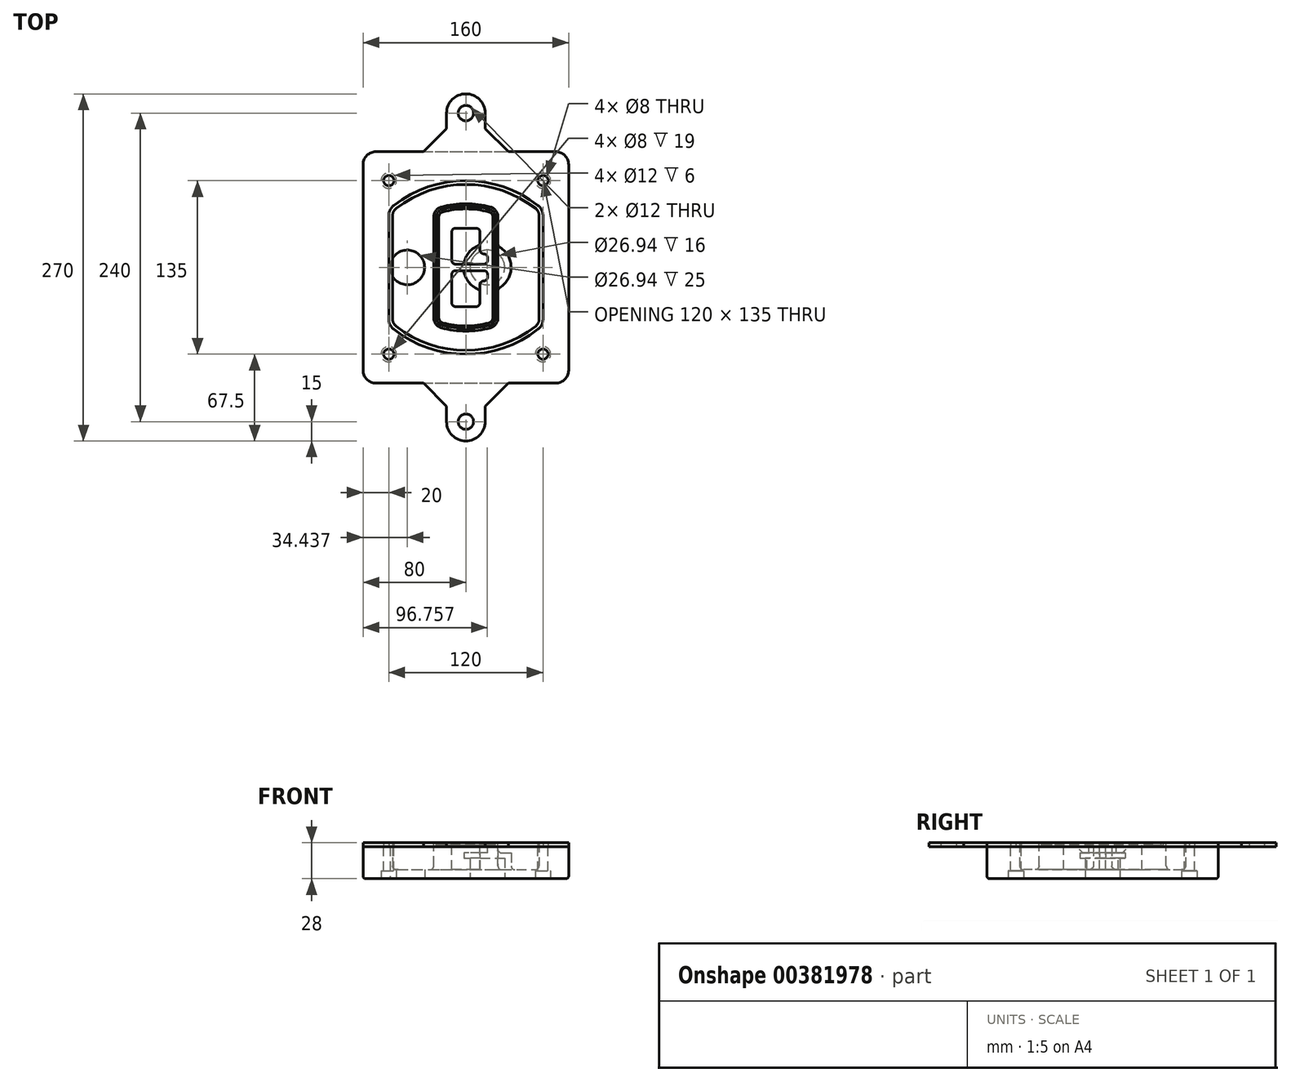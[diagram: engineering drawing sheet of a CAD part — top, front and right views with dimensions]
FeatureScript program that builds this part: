
annotation { "Feature Type Name" : "Feature", "Feature Type Description" : "" }
export const myFeature = defineFeature(function(context is Context, id is Id, definition is map)
    precondition{}
    {
        {
            var Q0;
            Q0=qCreatedBy(makeId("Top.planeOp"),FACE);
            var sketch = newSketch(context, id + "F0", { "sketchPlane" : qUnion([Q0])});
            skPoint(sketch, "E0.rect.middle", {"position": v(0, 0) * mm});
            skLineSegment(sketch, "E1.bottom", {"start": v(-70, -90) * mm, "end": v(70, -90) * mm});
            skLineSegment(sketch, "E1.top", {"start": v(-70, 90) * mm, "end": v(70, 90) * mm});
            skLineSegment(sketch, "E1.left", {"start": v(-80, -80) * mm, "end": v(-80, 80) * mm});
            skLineSegment(sketch, "E1.right", {"start": v(80, -80) * mm, "end": v(80, 80) * mm});
            skLineSegment(sketch, "E2", {"start": v(-80, 90) * mm, "end": v(80, -90) * mm, "construction": true});
            skLineSegment(sketch, "E3", {"start": v(80, 90) * mm, "end": v(-80, -90) * mm, "construction": true});
            skCircle(sketch, "E4", {"center": v(-60, 67.5) * mm, "radius": 4 * mm});
            skCircle(sketch, "E5", {"center": v(60, 67.5) * mm, "radius": 4 * mm});
            skCircle(sketch, "E6", {"center": v(60, -67.5) * mm, "radius": 4 * mm});
            skCircle(sketch, "E7", {"center": v(-60, -67.5) * mm, "radius": 4 * mm});
            skLineSegment(sketch, "E8", {"start": v(-60, 67.5) * mm, "end": v(60, 67.5) * mm, "construction": true});
            skLineSegment(sketch, "E9", {"start": v(60, 67.5) * mm, "end": v(60, -67.5) * mm, "construction": true});
            skLineSegment(sketch, "E10", {"start": v(60, -67.5) * mm, "end": v(-60, -67.5) * mm, "construction": true});
            skLineSegment(sketch, "E11", {"start": v(-60, -67.5) * mm, "end": v(-60, 67.5) * mm, "construction": true});
            skLineSegment(sketch, "E12", {"start": v(-60, 40.3) * mm, "end": v(-60, -40.3) * mm});
            skLineSegment(sketch, "E13", {"start": v(60, 40.3) * mm, "end": v(60, -40.3) * mm});
            skArc(sketch, "E14", {"start": v(56.15, 48.18) * mm, "mid": v(0, 67.5) * mm, "end": v(-56.15, 48.18) * mm});
            skArc(sketch, "E15", {"start": v(-56.15, -48.18) * mm, "mid": v(0, -67.5) * mm, "end": v(56.15, -48.18) * mm});
            skLineSegment(sketch, "E16", {"start": v(-60, 0) * mm, "end": v(60, 0) * mm, "construction": true});
            skPoint(sketch, "E17.visualSharp", {"position": v(-60, -45) * mm});
            skArc(sketch, "E17.filletArc", {"start": v(-60, -40.3) * mm, "mid": v(-58.99, -44.68) * mm, "end": v(-56.15, -48.18) * mm});
            skPoint(sketch, "E18.visualSharp", {"position": v(-60, 45) * mm});
            skArc(sketch, "E18.filletArc", {"start": v(-56.15, 48.18) * mm, "mid": v(-58.99, 44.68) * mm, "end": v(-60, 40.3) * mm});
            skPoint(sketch, "E19.visualSharp", {"position": v(60, 45) * mm});
            skArc(sketch, "E19.filletArc", {"start": v(60, 40.3) * mm, "mid": v(58.99, 44.68) * mm, "end": v(56.15, 48.18) * mm});
            skPoint(sketch, "E20.visualSharp", {"position": v(60, -45) * mm});
            skArc(sketch, "E20.filletArc", {"start": v(56.15, -48.18) * mm, "mid": v(58.99, -44.68) * mm, "end": v(60, -40.3) * mm});
            skPoint(sketch, "E21.visualSharp", {"position": v(-80, 90) * mm});
            skArc(sketch, "E21.filletArc", {"start": v(-70, 90) * mm, "mid": v(-77.07, 87.07) * mm, "end": v(-80, 80) * mm});
            skPoint(sketch, "E22.visualSharp", {"position": v(80, 90) * mm});
            skArc(sketch, "E22.filletArc", {"start": v(80, 80) * mm, "mid": v(77.07, 87.07) * mm, "end": v(70, 90) * mm});
            skPoint(sketch, "E23.visualSharp", {"position": v(80, -90) * mm});
            skArc(sketch, "E23.filletArc", {"start": v(70, -90) * mm, "mid": v(77.07, -87.07) * mm, "end": v(80, -80) * mm});
            skPoint(sketch, "E24.visualSharp", {"position": v(-80, -90) * mm});
            skArc(sketch, "E24.filletArc", {"start": v(-80, -80) * mm, "mid": v(-77.07, -87.07) * mm, "end": v(-70, -90) * mm});
            skArc(sketch, "E25.0", {"start": v(57, 40.3) * mm, "mid": v(56.3, 43.36) * mm, "end": v(54.3, 45.81) * mm});
            skLineSegment(sketch, "E25.1", {"start": v(57, 40.3) * mm, "end": v(57, -40.3) * mm});
            skArc(sketch, "E25.2", {"start": v(54.3, -45.81) * mm, "mid": v(56.3, -43.36) * mm, "end": v(57, -40.3) * mm});
            skArc(sketch, "E25.3", {"start": v(-54.3, -45.81) * mm, "mid": v(0, -64.5) * mm, "end": v(54.3, -45.81) * mm});
            skArc(sketch, "E25.4", {"start": v(-57, -40.3) * mm, "mid": v(-56.3, -43.36) * mm, "end": v(-54.3, -45.81) * mm});
            skArc(sketch, "E25.5", {"start": v(54.3, 45.81) * mm, "mid": v(0, 64.5) * mm, "end": v(-54.3, 45.81) * mm});
            skLineSegment(sketch, "E25.6", {"start": v(-57, 40.3) * mm, "end": v(-57, -40.3) * mm});
            skArc(sketch, "E25.7", {"start": v(-54.3, 45.81) * mm, "mid": v(-56.3, 43.36) * mm, "end": v(-57, 40.3) * mm});
            skArc(sketch, "E26.0", {"start": v(-58.62, 51.33) * mm, "mid": v(-62.58, 46.43) * mm, "end": v(-64, 40.3) * mm});
            skArc(sketch, "E26.1", {"start": v(58.62, 51.33) * mm, "mid": v(0, 71.5) * mm, "end": v(-58.62, 51.33) * mm});
            skArc(sketch, "E26.2", {"start": v(64, 40.3) * mm, "mid": v(62.58, 46.43) * mm, "end": v(58.62, 51.33) * mm});
            skLineSegment(sketch, "E26.3", {"start": v(64, 40.3) * mm, "end": v(64, -40.3) * mm});
            skArc(sketch, "E26.4", {"start": v(58.62, -51.33) * mm, "mid": v(62.58, -46.43) * mm, "end": v(64, -40.3) * mm});
            skLineSegment(sketch, "E26.5", {"start": v(-64, 40.3) * mm, "end": v(-64, -40.3) * mm});
            skArc(sketch, "E26.6", {"start": v(-58.62, -51.33) * mm, "mid": v(0, -71.5) * mm, "end": v(58.62, -51.33) * mm});
            skArc(sketch, "E26.7", {"start": v(-64, -40.3) * mm, "mid": v(-62.58, -46.43) * mm, "end": v(-58.62, -51.33) * mm});
            skSolve(sketch);
        }
        {
            var Q0;
            Q0=makeQuery(id+"F0.imprint","IMPRINT",FACE,{"disambiguationData":[TD([[makeQuery(id+"F0.imprint","IMPRINT",EDGE,{"derivedFrom":sQuery(id+"F0.wireOp",EDGE,"E1.bottom")}),1.0]])]});
            var Q1;
            Q1=makeQuery(id+"F0.imprint","IMPRINT",FACE,{"disambiguationData":[TD([[makeQuery(id+"F0.imprint","IMPRINT",EDGE,{"derivedFrom":sQuery(id+"F0.wireOp",EDGE,"E12")}),1.0]])]});
            var Q2;
            Q2=makeQuery(id+"F0.imprint","IMPRINT",FACE,{"disambiguationData":[TD([[makeQuery(id+"F0.imprint","IMPRINT",EDGE,{"derivedFrom":sQuery(id+"F0.wireOp",EDGE,"E25.0")}),1.0]])]});
            var Q3;
            Q3=makeQuery(id+"F0.imprint","IMPRINT",FACE,{"disambiguationData":[TD([[makeQuery(id+"F0.imprint","IMPRINT",EDGE,{"derivedFrom":sQuery(id+"F0.wireOp",EDGE,"E12")}),-1.0]])]});
            extrude(context, id + "F1", {"entities" : qUnion([Q0, Q1, Q2, Q3]), "oppositeDirection" : true, "depth" : 25 * mm});
        }
        {
            var Q0;
            Q0=makeQuery(id+"F0.imprint","IMPRINT",FACE,{"disambiguationData":[TD([[makeQuery(id+"F0.imprint","IMPRINT",EDGE,{"derivedFrom":sQuery(id+"F0.wireOp",EDGE,"E12")}),1.0]])]});
            extrude(context, id + "F2", {"entities" : qUnion([Q0]), "operationType" : NewBodyOperationType.ADD, "depth" : 3 * mm});
        }
        {
            var Q0;
            Q0=makeQuery(id+"F0.imprint","IMPRINT",FACE,{"disambiguationData":[TD([[makeQuery(id+"F0.imprint","IMPRINT",EDGE,{"derivedFrom":sQuery(id+"F0.wireOp",EDGE,"E25.0")}),1.0]])]});
            extrude(context, id + "F3", {"entities" : qUnion([Q0]), "operationType" : NewBodyOperationType.REMOVE, "oppositeDirection" : true, "depth" : 18 * mm});
        }
        {
            var Q0;
            Q0=makeQuery(id+"F2.opExtrude","CAP_FACE",FACE,{"disambiguationData":[OSD([sQuery(id+"F0.wireOp",EDGE,"E12"),sQuery(id+"F0.wireOp",EDGE,"E13"),sQuery(id+"F0.wireOp",EDGE,"E14"),sQuery(id+"F0.wireOp",EDGE,"E15"),sQuery(id+"F0.wireOp",EDGE,"E17.filletArc"),sQuery(id+"F0.wireOp",EDGE,"E18.filletArc"),sQuery(id+"F0.wireOp",EDGE,"E19.filletArc"),sQuery(id+"F0.wireOp",EDGE,"E20.filletArc"),sQuery(id+"F0.wireOp",EDGE,"E25.0"),sQuery(id+"F0.wireOp",EDGE,"E25.1"),sQuery(id+"F0.wireOp",EDGE,"E25.2"),sQuery(id+"F0.wireOp",EDGE,"E25.3"),sQuery(id+"F0.wireOp",EDGE,"E25.4"),sQuery(id+"F0.wireOp",EDGE,"E25.5"),sQuery(id+"F0.wireOp",EDGE,"E25.6"),sQuery(id+"F0.wireOp",EDGE,"E25.7")])],"isStart":false});
            var sketch = newSketch(context, id + "F4", { "sketchPlane" : qUnion([Q0])});
            skArc(sketch, "E27.0", {"start": v(-19.08, -46.97) * mm, "mid": v(0, -49.5) * mm, "end": v(19.08, -46.97) * mm});
            skArc(sketch, "E28.0", {"start": v(19.08, 46.97) * mm, "mid": v(0, 49.5) * mm, "end": v(-19.08, 46.97) * mm});
            skLineSegment(sketch, "E29", {"start": v(-25, 39.25) * mm, "end": v(-25, -39.25) * mm});
            skLineSegment(sketch, "E30", {"start": v(25, 39.25) * mm, "end": v(25, -39.25) * mm});
            skLineSegment(sketch, "E31", {"start": v(-25, 45.1) * mm, "end": v(25, 45.1) * mm, "construction": true});
            skLineSegment(sketch, "E32", {"start": v(-25, -45.1) * mm, "end": v(25, -45.1) * mm, "construction": true});
            skPoint(sketch, "E33.visualSharp", {"position": v(-25, 45.1) * mm});
            skArc(sketch, "E33.filletArc", {"start": v(-19.08, 46.97) * mm, "mid": v(-23.35, 44.11) * mm, "end": v(-25, 39.25) * mm});
            skPoint(sketch, "E34.visualSharp", {"position": v(25, 45.1) * mm});
            skArc(sketch, "E34.filletArc", {"start": v(25, 39.25) * mm, "mid": v(23.35, 44.11) * mm, "end": v(19.08, 46.97) * mm});
            skPoint(sketch, "E35.visualSharp", {"position": v(25, -45.1) * mm});
            skArc(sketch, "E35.filletArc", {"start": v(19.08, -46.97) * mm, "mid": v(23.35, -44.11) * mm, "end": v(25, -39.25) * mm});
            skPoint(sketch, "E36.visualSharp", {"position": v(-25, -45.1) * mm});
            skArc(sketch, "E36.filletArc", {"start": v(-25, -39.25) * mm, "mid": v(-23.35, -44.11) * mm, "end": v(-19.08, -46.97) * mm});
            skArc(sketch, "E37.0", {"start": v(54.3, 45.81) * mm, "mid": v(0, 64.5) * mm, "end": v(-54.3, 45.81) * mm});
            skArc(sketch, "E37.1", {"start": v(-54.3, 45.81) * mm, "mid": v(-56.3, 43.36) * mm, "end": v(-57, 40.3) * mm});
            skLineSegment(sketch, "E37.2", {"start": v(-57, 40.3) * mm, "end": v(-57, -40.3) * mm});
            skArc(sketch, "E37.3", {"start": v(-57, -40.3) * mm, "mid": v(-56.3, -43.36) * mm, "end": v(-54.3, -45.81) * mm});
            skArc(sketch, "E37.4", {"start": v(-54.3, -45.81) * mm, "mid": v(0, -64.5) * mm, "end": v(54.3, -45.81) * mm});
            skArc(sketch, "E37.5", {"start": v(54.3, -45.81) * mm, "mid": v(56.3, -43.36) * mm, "end": v(57, -40.3) * mm});
            skLineSegment(sketch, "E37.6", {"start": v(57, 40.3) * mm, "end": v(57, -40.3) * mm});
            skArc(sketch, "E37.7", {"start": v(57, 40.3) * mm, "mid": v(56.3, 43.36) * mm, "end": v(54.3, 45.81) * mm});
            skLineSegment(sketch, "E38.0", {"start": v(23, 39.25) * mm, "end": v(23, -39.25) * mm});
            skArc(sketch, "E38.1", {"start": v(18.56, -45.04) * mm, "mid": v(21.76, -42.9) * mm, "end": v(23, -39.25) * mm});
            skArc(sketch, "E38.2", {"start": v(-18.56, -45.04) * mm, "mid": v(0, -47.5) * mm, "end": v(18.56, -45.04) * mm});
            skArc(sketch, "E38.3", {"start": v(-23, -39.25) * mm, "mid": v(-21.76, -42.9) * mm, "end": v(-18.56, -45.04) * mm});
            skLineSegment(sketch, "E38.4", {"start": v(-23, 39.25) * mm, "end": v(-23, -39.25) * mm});
            skArc(sketch, "E38.5", {"start": v(23, 39.25) * mm, "mid": v(21.76, 42.9) * mm, "end": v(18.56, 45.04) * mm});
            skArc(sketch, "E38.6", {"start": v(-18.56, 45.04) * mm, "mid": v(-21.76, 42.9) * mm, "end": v(-23, 39.25) * mm});
            skArc(sketch, "E38.7", {"start": v(18.56, 45.04) * mm, "mid": v(0, 47.5) * mm, "end": v(-18.56, 45.04) * mm});
            skArc(sketch, "E39.0", {"start": v(21, 39.25) * mm, "mid": v(20.18, 41.68) * mm, "end": v(18.04, 43.1) * mm});
            skLineSegment(sketch, "E39.1", {"start": v(21, 39.25) * mm, "end": v(21, -39.25) * mm});
            skArc(sketch, "E39.2", {"start": v(18.04, -43.1) * mm, "mid": v(20.18, -41.68) * mm, "end": v(21, -39.25) * mm});
            skArc(sketch, "E39.3", {"start": v(-18.04, -43.1) * mm, "mid": v(0, -45.5) * mm, "end": v(18.04, -43.1) * mm});
            skArc(sketch, "E39.4", {"start": v(-21, -39.25) * mm, "mid": v(-20.18, -41.68) * mm, "end": v(-18.04, -43.1) * mm});
            skArc(sketch, "E39.5", {"start": v(18.04, 43.1) * mm, "mid": v(0, 45.5) * mm, "end": v(-18.04, 43.1) * mm});
            skLineSegment(sketch, "E39.6", {"start": v(-21, 39.25) * mm, "end": v(-21, -39.25) * mm});
            skArc(sketch, "E39.7", {"start": v(-18.04, 43.1) * mm, "mid": v(-20.18, 41.68) * mm, "end": v(-21, 39.25) * mm});
            skLineSegment(sketch, "E40", {"start": v(-25, 0) * mm, "end": v(25, 0) * mm, "construction": true});
            skLineSegment(sketch, "E41", {"start": v(-11, 5.5) * mm, "end": v(-11, 27.5) * mm});
            skLineSegment(sketch, "E42", {"start": v(-8, 30.5) * mm, "end": v(8, 30.5) * mm});
            skLineSegment(sketch, "E43", {"start": v(11, 27.5) * mm, "end": v(11, 13.5) * mm});
            skLineSegment(sketch, "E44", {"start": v(14, 10.5) * mm, "end": v(14, 10.5) * mm});
            skLineSegment(sketch, "E45", {"start": v(17, 7.5) * mm, "end": v(17, 5.5) * mm});
            skLineSegment(sketch, "E46", {"start": v(14, 2.5) * mm, "end": v(-8, 2.5) * mm});
            skPoint(sketch, "E47.visualSharp", {"position": v(-11, 30.5) * mm});
            skArc(sketch, "E47.filletArc", {"start": v(-8, 30.5) * mm, "mid": v(-10.12, 29.62) * mm, "end": v(-11, 27.5) * mm});
            skPoint(sketch, "E48.visualSharp", {"position": v(11, 30.5) * mm});
            skArc(sketch, "E48.filletArc", {"start": v(11, 27.5) * mm, "mid": v(10.12, 29.62) * mm, "end": v(8, 30.5) * mm});
            skPoint(sketch, "E49.visualSharp", {"position": v(11, 10.5) * mm});
            skArc(sketch, "E49.filletArc", {"start": v(11, 13.5) * mm, "mid": v(11.88, 11.38) * mm, "end": v(14, 10.5) * mm});
            skPoint(sketch, "E50.visualSharp", {"position": v(17, 10.5) * mm});
            skArc(sketch, "E50.filletArc", {"start": v(17, 7.5) * mm, "mid": v(16.12, 9.62) * mm, "end": v(14, 10.5) * mm});
            skPoint(sketch, "E51.visualSharp", {"position": v(17, 2.5) * mm});
            skArc(sketch, "E51.filletArc", {"start": v(14, 2.5) * mm, "mid": v(16.12, 3.38) * mm, "end": v(17, 5.5) * mm});
            skPoint(sketch, "E52.visualSharp", {"position": v(-11, 2.5) * mm});
            skArc(sketch, "E52.filletArc", {"start": v(-11, 5.5) * mm, "mid": v(-10.12, 3.38) * mm, "end": v(-8, 2.5) * mm});
            skLineSegment(sketch, "E53.0.MirrorCS", {"start": v(14, -2.5) * mm, "end": v(-8, -2.5) * mm});
            skArc(sketch, "E54.0.MirrorCS", {"start": v(-11, -5.5) * mm, "mid": v(-10.12, -3.38) * mm, "end": v(-8, -2.5) * mm});
            skLineSegment(sketch, "E55.0.MirrorCS", {"start": v(-11, -5.5) * mm, "end": v(-11, -27.5) * mm});
            skArc(sketch, "E56.0.MirrorCS", {"start": v(-8, -30.5) * mm, "mid": v(-10.12, -29.62) * mm, "end": v(-11, -27.5) * mm});
            skLineSegment(sketch, "E57.0.MirrorCS", {"start": v(-8, -30.5) * mm, "end": v(8, -30.5) * mm});
            skArc(sketch, "E58.0.MirrorCS", {"start": v(11, -27.5) * mm, "mid": v(10.12, -29.62) * mm, "end": v(8, -30.5) * mm});
            skLineSegment(sketch, "E59.0.MirrorCS", {"start": v(11, -27.5) * mm, "end": v(11, -13.5) * mm});
            skArc(sketch, "E60.0.MirrorCS", {"start": v(11, -13.5) * mm, "mid": v(11.88, -11.38) * mm, "end": v(14, -10.5) * mm});
            skArc(sketch, "E61.0.MirrorCS", {"start": v(17, -7.5) * mm, "mid": v(16.12, -9.62) * mm, "end": v(14, -10.5) * mm});
            skLineSegment(sketch, "E62.0.MirrorCS", {"start": v(17, -7.5) * mm, "end": v(17, -5.5) * mm});
            skArc(sketch, "E63.0.MirrorCS", {"start": v(14, -2.5) * mm, "mid": v(16.12, -3.38) * mm, "end": v(17, -5.5) * mm});
            skSolve(sketch);
        }
        {
            var Q0;
            Q0=makeQuery(id+"F4.imprint","IMPRINT",FACE,{"disambiguationData":[TD([[makeQuery(id+"F4.imprint","IMPRINT",EDGE,{"derivedFrom":sQuery(id+"F4.wireOp",EDGE,"E27.0")}),1.0]])]});
            var Q1;
            Q1=makeQuery(id+"F4.imprint","IMPRINT",FACE,{"disambiguationData":[TD([[makeQuery(id+"F4.imprint","IMPRINT",EDGE,{"derivedFrom":sQuery(id+"F4.wireOp",EDGE,"E38.0")}),-1.0]])]});
            var Q2;
            Q2=makeQuery(id+"F4.imprint","IMPRINT",FACE,{"disambiguationData":[TD([[makeQuery(id+"F4.imprint","IMPRINT",EDGE,{"derivedFrom":sQuery(id+"F4.wireOp",EDGE,"E39.0")}),1.0]])]});
            extrude(context, id + "F5", {"entities" : qUnion([Q0, Q1, Q2]), "operationType" : NewBodyOperationType.ADD, "endBound" : BoundingType.UP_TO_NEXT, "oppositeDirection" : true, "depth" : 25 * mm});
        }
        {
            var Q0;
            Q0=makeQuery(id+"F4.imprint","IMPRINT",FACE,{"disambiguationData":[TD([[makeQuery(id+"F4.imprint","IMPRINT",EDGE,{"derivedFrom":sQuery(id+"F4.wireOp",EDGE,"E38.0")}),-1.0]])]});
            extrude(context, id + "F6", {"entities" : qUnion([Q0]), "operationType" : NewBodyOperationType.REMOVE, "oppositeDirection" : true, "depth" : 2 * mm});
        }
        {
            var Q0;
            Q0=makeQuery(id+"F1.opExtrude","CAP_FACE",FACE,{"disambiguationData":[OSD([sQuery(id+"F0.wireOp",EDGE,"E1.bottom"),sQuery(id+"F0.wireOp",EDGE,"E1.top"),sQuery(id+"F0.wireOp",EDGE,"E1.left"),sQuery(id+"F0.wireOp",EDGE,"E1.right"),sQuery(id+"F0.wireOp",EDGE,"E4"),sQuery(id+"F0.wireOp",EDGE,"E5"),sQuery(id+"F0.wireOp",EDGE,"E6"),sQuery(id+"F0.wireOp",EDGE,"E7"),sQuery(id+"F0.wireOp",EDGE,"E21.filletArc"),sQuery(id+"F0.wireOp",EDGE,"E22.filletArc"),sQuery(id+"F0.wireOp",EDGE,"E23.filletArc"),sQuery(id+"F0.wireOp",EDGE,"E24.filletArc")])],"isStart":false});
            var sketch = newSketch(context, id + "F7", { "sketchPlane" : qUnion([Q0])});
            skCircle(sketch, "E64", {"center": v(16.76, 0) * mm, "radius": 13.47 * mm});
            skCircle(sketch, "E65", {"center": v(-45.56, 0) * mm, "radius": 13.47 * mm});
            skLineSegment(sketch, "E66", {"start": v(80, 0) * mm, "end": v(-80, 0) * mm});
            skCircle(sketch, "E67", {"center": v(16.76, 0) * mm, "radius": 18.47 * mm});
            skCircle(sketch, "E68", {"center": v(60, -67.5) * mm, "radius": 6 * mm});
            skCircle(sketch, "E69", {"center": v(-60, -67.5) * mm, "radius": 6 * mm});
            skCircle(sketch, "E70", {"center": v(-60, 67.5) * mm, "radius": 6 * mm});
            skCircle(sketch, "E71", {"center": v(60, 67.5) * mm, "radius": 6 * mm});
            skSolve(sketch);
        }
        {
            var Q0;
            {var subQ1=sQuery(id+"F7.wireOp",EDGE,"E66");var subQ4=sQuery(id+"F7.wireOp",EDGE,"E64");var subQ6=makeQuery(id+"F7.imprint","INTERSECT",VERTEX,{"disambiguationData":[OD(0.0)],"derivedFrom":[subQ4,subQ1]});Q0=makeQuery(id+"F7.imprint","IMPRINT",FACE,{"disambiguationData":[TD([[makeQuery(id+"F7.imprint","IMPRINT",EDGE,{"disambiguationData":[TD([[subQ6,-1.0]])],"derivedFrom":subQ4}),-1.0]])]});}
            var Q1;
            {var subQ0=sQuery(id+"F7.wireOp",EDGE,"E66");var subQ1=sQuery(id+"F7.wireOp",EDGE,"E64");var subQ3=makeQuery(id+"F7.imprint","INTERSECT",VERTEX,{"disambiguationData":[OD(0.0)],"derivedFrom":[subQ1,subQ0]});Q1=makeQuery(id+"F7.imprint","IMPRINT",FACE,{"disambiguationData":[TD([[makeQuery(id+"F7.imprint","IMPRINT",EDGE,{"disambiguationData":[TD([[subQ3,-1.0]])],"derivedFrom":subQ1}),1.0]])]});}
            var Q2;
            {var subQ0=sQuery(id+"F7.wireOp",EDGE,"E66");var subQ1=sQuery(id+"F7.wireOp",EDGE,"E64");var subQ3=makeQuery(id+"F7.imprint","INTERSECT",VERTEX,{"disambiguationData":[OD(0.0)],"derivedFrom":[subQ1,subQ0]});Q2=makeQuery(id+"F7.imprint","IMPRINT",FACE,{"disambiguationData":[TD([[makeQuery(id+"F7.imprint","IMPRINT",EDGE,{"disambiguationData":[TD([[subQ3,1.0]])],"derivedFrom":subQ1}),1.0]])]});}
            var Q3;
            {var subQ1=sQuery(id+"F7.wireOp",EDGE,"E66");var subQ4=sQuery(id+"F7.wireOp",EDGE,"E64");var subQ6=makeQuery(id+"F7.imprint","INTERSECT",VERTEX,{"disambiguationData":[OD(0.0)],"derivedFrom":[subQ4,subQ1]});Q3=makeQuery(id+"F7.imprint","IMPRINT",FACE,{"disambiguationData":[TD([[makeQuery(id+"F7.imprint","IMPRINT",EDGE,{"disambiguationData":[TD([[subQ6,1.0]])],"derivedFrom":subQ4}),-1.0]])]});}
            extrude(context, id + "F8", {"entities" : qUnion([Q0, Q1, Q2, Q3]), "operationType" : NewBodyOperationType.ADD, "oppositeDirection" : true, "depth" : 20 * mm});
        }
        {
            var Q0;
            {var subQ0=sQuery(id+"F7.wireOp",EDGE,"E66");var subQ1=sQuery(id+"F7.wireOp",EDGE,"E64");var subQ3=makeQuery(id+"F7.imprint","INTERSECT",VERTEX,{"disambiguationData":[OD(0.0)],"derivedFrom":[subQ1,subQ0]});Q0=makeQuery(id+"F7.imprint","IMPRINT",FACE,{"disambiguationData":[TD([[makeQuery(id+"F7.imprint","IMPRINT",EDGE,{"disambiguationData":[TD([[subQ3,-1.0]])],"derivedFrom":subQ1}),1.0]])]});}
            var Q1;
            {var subQ0=sQuery(id+"F7.wireOp",EDGE,"E66");var subQ1=sQuery(id+"F7.wireOp",EDGE,"E64");var subQ3=makeQuery(id+"F7.imprint","INTERSECT",VERTEX,{"disambiguationData":[OD(0.0)],"derivedFrom":[subQ1,subQ0]});Q1=makeQuery(id+"F7.imprint","IMPRINT",FACE,{"disambiguationData":[TD([[makeQuery(id+"F7.imprint","IMPRINT",EDGE,{"disambiguationData":[TD([[subQ3,1.0]])],"derivedFrom":subQ1}),1.0]])]});}
            extrude(context, id + "F9", {"entities" : qUnion([Q0, Q1]), "operationType" : NewBodyOperationType.REMOVE, "oppositeDirection" : true, "depth" : 16 * mm});
        }
        {
            var Q0;
            {var subQ0=sQuery(id+"F7.wireOp",EDGE,"E66");var subQ1=sQuery(id+"F7.wireOp",EDGE,"E65");var subQ3=makeQuery(id+"F7.imprint","INTERSECT",VERTEX,{"disambiguationData":[OD(0.0)],"derivedFrom":[subQ1,subQ0]});Q0=makeQuery(id+"F7.imprint","IMPRINT",FACE,{"disambiguationData":[TD([[makeQuery(id+"F7.imprint","IMPRINT",EDGE,{"disambiguationData":[TD([[subQ3,-1.0]])],"derivedFrom":subQ1}),1.0]])]});}
            var Q1;
            {var subQ0=sQuery(id+"F7.wireOp",EDGE,"E66");var subQ1=sQuery(id+"F7.wireOp",EDGE,"E65");var subQ3=makeQuery(id+"F7.imprint","INTERSECT",VERTEX,{"disambiguationData":[OD(0.0)],"derivedFrom":[subQ1,subQ0]});Q1=makeQuery(id+"F7.imprint","IMPRINT",FACE,{"disambiguationData":[TD([[makeQuery(id+"F7.imprint","IMPRINT",EDGE,{"disambiguationData":[TD([[subQ3,1.0]])],"derivedFrom":subQ1}),1.0]])]});}
            extrude(context, id + "F10", {"entities" : qUnion([Q0, Q1]), "operationType" : NewBodyOperationType.REMOVE, "oppositeDirection" : true, "depth" : 25 * mm});
        }
        {
            var Q0;
            Q0=makeQuery(id+"F7.imprint","IMPRINT",FACE,{"disambiguationData":[TD([[makeQuery(id+"F7.imprint","IMPRINT",EDGE,{"derivedFrom":sQuery(id+"F7.wireOp",EDGE,"E68")}),1.0]])]});
            var Q1;
            Q1=makeQuery(id+"F7.imprint","IMPRINT",FACE,{"disambiguationData":[TD([[makeQuery(id+"F7.imprint","IMPRINT",EDGE,{"derivedFrom":makeQuery(id+"F1.opExtrude","CAP_EDGE",EDGE,{"disambiguationData":[OSD([sQuery(id+"F0.wireOp",EDGE,"E5")])],"isStart":false})}),-1.0]])]});
            var Q2;
            Q2=makeQuery(id+"F7.imprint","IMPRINT",FACE,{"disambiguationData":[TD([[makeQuery(id+"F7.imprint","IMPRINT",EDGE,{"derivedFrom":sQuery(id+"F7.wireOp",EDGE,"E69")}),1.0]])]});
            var Q3;
            Q3=makeQuery(id+"F7.imprint","IMPRINT",FACE,{"disambiguationData":[TD([[makeQuery(id+"F7.imprint","IMPRINT",EDGE,{"derivedFrom":makeQuery(id+"F1.opExtrude","CAP_EDGE",EDGE,{"disambiguationData":[OSD([sQuery(id+"F0.wireOp",EDGE,"E4")])],"isStart":false})}),-1.0]])]});
            var Q4;
            Q4=makeQuery(id+"F7.imprint","IMPRINT",FACE,{"disambiguationData":[TD([[makeQuery(id+"F7.imprint","IMPRINT",EDGE,{"derivedFrom":sQuery(id+"F7.wireOp",EDGE,"E70")}),1.0]])]});
            var Q5;
            Q5=makeQuery(id+"F7.imprint","IMPRINT",FACE,{"disambiguationData":[TD([[makeQuery(id+"F7.imprint","IMPRINT",EDGE,{"derivedFrom":makeQuery(id+"F1.opExtrude","CAP_EDGE",EDGE,{"disambiguationData":[OSD([sQuery(id+"F0.wireOp",EDGE,"E7")])],"isStart":false})}),-1.0]])]});
            var Q6;
            Q6=makeQuery(id+"F7.imprint","IMPRINT",FACE,{"disambiguationData":[TD([[makeQuery(id+"F7.imprint","IMPRINT",EDGE,{"derivedFrom":sQuery(id+"F7.wireOp",EDGE,"E71")}),1.0]])]});
            var Q7;
            Q7=makeQuery(id+"F7.imprint","IMPRINT",FACE,{"disambiguationData":[TD([[makeQuery(id+"F7.imprint","IMPRINT",EDGE,{"derivedFrom":makeQuery(id+"F1.opExtrude","CAP_EDGE",EDGE,{"disambiguationData":[OSD([sQuery(id+"F0.wireOp",EDGE,"E6")])],"isStart":false})}),-1.0]])]});
            extrude(context, id + "F11", {"entities" : qUnion([Q0, Q1, Q2, Q3, Q4, Q5, Q6, Q7]), "operationType" : NewBodyOperationType.REMOVE, "oppositeDirection" : true, "depth" : 6 * mm});
        }
        {
            var Q0;
            Q0=makeQuery(id+"F9.boolean.opBoolean","COPY",FACE,{"derivedFrom":makeQuery(id+"F9.opExtrude","CAP_FACE",FACE,{"disambiguationData":[OSD([sQuery(id+"F7.wireOp",EDGE,"E64")])],"isStart":false})});
            var sketch = newSketch(context, id + "F12", { "sketchPlane" : qUnion([Q0])});
            skArc(sketch, "E72.0", {"start": v(11, 17.55) * mm, "mid": v(2.57, 11.82) * mm, "end": v(-1.54, 2.5) * mm});
            skArc(sketch, "E72.1", {"start": v(-1.54, -2.5) * mm, "mid": v(2.57, -11.82) * mm, "end": v(11, -17.55) * mm});
            skLineSegment(sketch, "E73", {"start": v(-1.54, -2.5) * mm, "end": v(14, -2.5) * mm});
            skLineSegment(sketch, "E74.0", {"start": v(14, 2.5) * mm, "end": v(-1.54, 2.5) * mm});
            skArc(sketch, "E74.1", {"start": v(14, 2.5) * mm, "mid": v(16.12, 3.38) * mm, "end": v(17, 5.5) * mm});
            skLineSegment(sketch, "E74.2", {"start": v(17, 7.5) * mm, "end": v(17, 5.5) * mm});
            skArc(sketch, "E74.3", {"start": v(17, 7.5) * mm, "mid": v(16.12, 9.62) * mm, "end": v(14, 10.5) * mm});
            skArc(sketch, "E74.4", {"start": v(11, 13.5) * mm, "mid": v(11.88, 11.38) * mm, "end": v(14, 10.5) * mm});
            skLineSegment(sketch, "E74.5", {"start": v(11, 17.55) * mm, "end": v(11, 13.5) * mm});
            skLineSegment(sketch, "E74.7", {"start": v(14, -2.5) * mm, "end": v(-1.54, -2.5) * mm});
            skArc(sketch, "E74.8", {"start": v(14, -2.5) * mm, "mid": v(16.12, -3.38) * mm, "end": v(17, -5.5) * mm});
            skLineSegment(sketch, "E74.9", {"start": v(17, -7.5) * mm, "end": v(17, -5.5) * mm});
            skArc(sketch, "E74.10", {"start": v(17, -7.5) * mm, "mid": v(16.12, -9.62) * mm, "end": v(14, -10.5) * mm});
            skArc(sketch, "E74.11", {"start": v(11, -13.5) * mm, "mid": v(11.88, -11.38) * mm, "end": v(14, -10.5) * mm});
            skLineSegment(sketch, "E74.12", {"start": v(11, -17.55) * mm, "end": v(11, -13.5) * mm});
            skPoint(sketch, "E75.orphan", {"position": v(11, -27.5) * mm});
            skPoint(sketch, "E76.orphan", {"position": v(-8, -2.5) * mm});
            skPoint(sketch, "E77.orphan", {"position": v(-8, 2.5) * mm});
            skPoint(sketch, "E78.orphan", {"position": v(11, 27.5) * mm});
            skSolve(sketch);
        }
        {
            var Q0;
            {var subQ7=sQuery(id+"F12.wireOp",EDGE,"E72.0");var subQ14=sQuery(id+"F12.wireOp",EDGE,"E72.1");var subQ16=sQuery(id+"F12.wireOp",EDGE,"E74.1");var subQ18=sQuery(id+"F12.wireOp",EDGE,"E74.8");Q0=qUnion([makeQuery(id+"F12.imprint","IMPRINT",FACE,{"disambiguationData":[TD([[makeQuery(id+"F12.imprint","IMPRINT",EDGE,{"derivedFrom":subQ7}),1.0]])]}),makeQuery(id+"F12.imprint","IMPRINT",FACE,{"disambiguationData":[TD([[makeQuery(id+"F12.imprint","IMPRINT",EDGE,{"derivedFrom":subQ14}),1.0]])]}),makeQuery(id+"F12.imprint","IMPRINT",FACE,{"disambiguationData":[TD([[makeQuery(id+"F12.imprint","IMPRINT",EDGE,{"derivedFrom":subQ16}),1.0]])]}),makeQuery(id+"F12.imprint","IMPRINT",FACE,{"disambiguationData":[TD([[makeQuery(id+"F12.imprint","IMPRINT",EDGE,{"derivedFrom":subQ18}),-1.0]])]})]);}
            var Q1;
            Q1=makeQuery(id+"F5.boolean.opBoolean","SPLIT",FACE,{"disambiguationData":[TD([makeQuery(id+"F5.opExtrude","SWEPT_FACE",FACE,{"disambiguationData":[OSD([sQuery(id+"F4.wireOp",EDGE,"E41")])]})])],"derivedFrom":makeQuery(id+"F3.boolean.opBoolean","COPY",FACE,{"derivedFrom":makeQuery(id+"F3.opExtrude","CAP_FACE",FACE,{"disambiguationData":[OSD([sQuery(id+"F0.wireOp",EDGE,"E25.0"),sQuery(id+"F0.wireOp",EDGE,"E25.1"),sQuery(id+"F0.wireOp",EDGE,"E25.2"),sQuery(id+"F0.wireOp",EDGE,"E25.3"),sQuery(id+"F0.wireOp",EDGE,"E25.4"),sQuery(id+"F0.wireOp",EDGE,"E25.5"),sQuery(id+"F0.wireOp",EDGE,"E25.6"),sQuery(id+"F0.wireOp",EDGE,"E25.7")])],"isStart":false})})});
            extrude(context, id + "F13", {"entities" : qUnion([Q0]), "operationType" : NewBodyOperationType.REMOVE, "endBound" : BoundingType.UP_TO_SURFACE, "endBoundEntityFace" : qUnion([Q1]), "depth" : 25 * mm});
        }
        {
            var Q0;
            Q0=makeQuery(id+"F3.boolean.opBoolean","COPY",EDGE,{"derivedFrom":makeQuery(id+"F3.opExtrude","CAP_EDGE",EDGE,{"disambiguationData":[OSD([sQuery(id+"F0.wireOp",EDGE,"E25.6")])],"isStart":false})});
            var Q1;
            Q1=makeQuery(id+"F8.boolean.opBoolean","INTERSECT",EDGE,{"derivedFrom":[makeQuery(id+"F5.opExtrude","SWEPT_FACE",FACE,{"disambiguationData":[OSD([sQuery(id+"F4.wireOp",EDGE,"E30")])]}),makeQuery(id+"F8.opExtrude","CAP_FACE",FACE,{"disambiguationData":[OSD([sQuery(id+"F7.wireOp",EDGE,"E67")])],"isStart":false})]});
            var Q2;
            Q2=makeQuery(id+"F8.boolean.opBoolean","INTERSECT",EDGE,{"disambiguationData":[OD(1.0)],"derivedFrom":[makeQuery(id+"F5.opExtrude","SWEPT_FACE",FACE,{"disambiguationData":[OSD([sQuery(id+"F4.wireOp",EDGE,"E30")])]}),makeQuery(id+"F8.opExtrude","SWEPT_FACE",FACE,{"disambiguationData":[OSD([sQuery(id+"F7.wireOp",EDGE,"E67")])]})]});
            var Q3;
            {var subQ0=sQuery(id+"F4.wireOp",EDGE,"E30");Q3=makeQuery(id+"F8.boolean.opBoolean","SPLIT",EDGE,{"disambiguationData":[TD([makeQuery(id+"F5.opExtrude","SWEPT_FACE",FACE,{"disambiguationData":[OSD([sQuery(id+"F4.wireOp",EDGE,"E35.filletArc")])]})])],"derivedFrom":makeQuery(id+"F5.opExtrude","CAP_EDGE",EDGE,{"disambiguationData":[OSD([subQ0])],"isStart":false})});}
            var Q4;
            {var subQ0=sQuery(id+"F0.wireOp",EDGE,"E25.7");var subQ1=sQuery(id+"F0.wireOp",EDGE,"E25.1");var subQ2=sQuery(id+"F0.wireOp",EDGE,"E25.6");var subQ3=sQuery(id+"F0.wireOp",EDGE,"E25.5");var subQ4=sQuery(id+"F0.wireOp",EDGE,"E25.4");var subQ5=sQuery(id+"F0.wireOp",EDGE,"E25.0");var subQ6=sQuery(id+"F0.wireOp",EDGE,"E25.2");var subQ7=sQuery(id+"F0.wireOp",EDGE,"E25.3");Q4=makeQuery(id+"F8.boolean.opBoolean","INTERSECT",EDGE,{"derivedFrom":[makeQuery(id+"F5.boolean.opBoolean","SPLIT",FACE,{"disambiguationData":[TD([makeQuery(id+"F2.opExtrude","SWEPT_FACE",FACE,{"disambiguationData":[OSD([subQ5])]})])],"derivedFrom":makeQuery(id+"F3.boolean.opBoolean","COPY",FACE,{"derivedFrom":makeQuery(id+"F3.opExtrude","CAP_FACE",FACE,{"disambiguationData":[OSD([subQ5,subQ1,subQ6,subQ7,subQ4,subQ3,subQ2,subQ0])],"isStart":false})})}),makeQuery(id+"F8.opExtrude","SWEPT_FACE",FACE,{"disambiguationData":[OSD([sQuery(id+"F7.wireOp",EDGE,"E67")])]})]});}
            var Q5;
            Q5=makeQuery(id+"F8.boolean.opBoolean","INTERSECT",EDGE,{"disambiguationData":[OD(0.0)],"derivedFrom":[makeQuery(id+"F5.opExtrude","SWEPT_FACE",FACE,{"disambiguationData":[OSD([sQuery(id+"F4.wireOp",EDGE,"E30")])]}),makeQuery(id+"F8.opExtrude","SWEPT_FACE",FACE,{"disambiguationData":[OSD([sQuery(id+"F7.wireOp",EDGE,"E67")])]})]});
            fillet(context, id + "F14", {"entities" : qUnion([Q0, Q1, Q2, Q3, Q4, Q5]), "radius" : 3 * mm, "tangentPropagation" : true, "allowEdgeOverflow" : false});
        }
        {
            var Q0;
            Q0=makeQuery(id+"F1.opExtrude","CAP_EDGE",EDGE,{"disambiguationData":[OSD([sQuery(id+"F0.wireOp",EDGE,"E1.bottom")])],"isStart":false});
            fillet(context, id + "F15", {"entities" : qUnion([Q0]), "radius" : 2 * mm, "tangentPropagation" : true, "allowEdgeOverflow" : false});
        }
        {
            var Q0;
            {var subQ0=sQuery(id+"F0.wireOp",EDGE,"E21.filletArc");var subQ1=sQuery(id+"F0.wireOp",EDGE,"E7");var subQ2=sQuery(id+"F0.wireOp",EDGE,"E6");var subQ3=sQuery(id+"F0.wireOp",EDGE,"E5");var subQ4=sQuery(id+"F0.wireOp",EDGE,"E4");var subQ5=sQuery(id+"F0.wireOp",EDGE,"E22.filletArc");var subQ6=sQuery(id+"F0.wireOp",EDGE,"E1.bottom");var subQ7=sQuery(id+"F0.wireOp",EDGE,"E1.right");var subQ8=sQuery(id+"F0.wireOp",EDGE,"E1.top");var subQ9=sQuery(id+"F0.wireOp",EDGE,"E1.left");var subQ10=sQuery(id+"F0.wireOp",EDGE,"E23.filletArc");var subQ11=sQuery(id+"F0.wireOp",EDGE,"E24.filletArc");Q0=makeQuery(id+"F2.boolean.opBoolean","SPLIT",FACE,{"disambiguationData":[TD([makeQuery(id+"F1.opExtrude","SWEPT_FACE",FACE,{"disambiguationData":[OSD([subQ6])]})])],"derivedFrom":makeQuery(id+"F1.opExtrude","CAP_FACE",FACE,{"disambiguationData":[OSD([subQ6,subQ8,subQ9,subQ7,subQ4,subQ3,subQ2,subQ1,subQ0,subQ5,subQ10,subQ11])],"isStart":true})});}
            var sketch = newSketch(context, id + "F16", { "sketchPlane" : qUnion([Q0])});
            skLineSegment(sketch, "E79.0", {"start": v(-70, 90) * mm, "end": v(70, 90) * mm});
            skArc(sketch, "E79.1", {"start": v(80, 80) * mm, "mid": v(77.07, 87.07) * mm, "end": v(70, 90) * mm});
            skLineSegment(sketch, "E79.2", {"start": v(80, -80) * mm, "end": v(80, 80) * mm});
            skArc(sketch, "E79.3", {"start": v(70, -90) * mm, "mid": v(77.07, -87.07) * mm, "end": v(80, -80) * mm});
            skLineSegment(sketch, "E79.4", {"start": v(-70, -90) * mm, "end": v(70, -90) * mm});
            skArc(sketch, "E79.5", {"start": v(-80, -80) * mm, "mid": v(-77.07, -87.07) * mm, "end": v(-70, -90) * mm});
            skLineSegment(sketch, "E79.6", {"start": v(-80, -80) * mm, "end": v(-80, 80) * mm});
            skArc(sketch, "E79.7", {"start": v(-70, 90) * mm, "mid": v(-77.07, 87.07) * mm, "end": v(-80, 80) * mm});
            skCircle(sketch, "E79.8", {"center": v(-60, 67.5) * mm, "radius": 4 * mm});
            skCircle(sketch, "E79.9", {"center": v(60, 67.5) * mm, "radius": 4 * mm});
            skCircle(sketch, "E79.10", {"center": v(60, -67.5) * mm, "radius": 4 * mm});
            skCircle(sketch, "E79.11", {"center": v(-60, -67.5) * mm, "radius": 4 * mm});
            skLineSegment(sketch, "E79.12", {"start": v(-60, 40.3) * mm, "end": v(-60, -40.3) * mm});
            skArc(sketch, "E79.13", {"start": v(-56.15, 48.18) * mm, "mid": v(-58.99, 44.68) * mm, "end": v(-60, 40.3) * mm});
            skArc(sketch, "E79.14", {"start": v(-60, -40.3) * mm, "mid": v(-58.99, -44.68) * mm, "end": v(-56.15, -48.18) * mm});
            skArc(sketch, "E79.15", {"start": v(56.15, 48.18) * mm, "mid": v(0, 67.5) * mm, "end": v(-56.15, 48.18) * mm});
            skArc(sketch, "E79.16", {"start": v(60, 40.3) * mm, "mid": v(58.99, 44.68) * mm, "end": v(56.15, 48.18) * mm});
            skLineSegment(sketch, "E79.17", {"start": v(60, 40.3) * mm, "end": v(60, -40.3) * mm});
            skArc(sketch, "E79.18", {"start": v(56.15, -48.18) * mm, "mid": v(58.99, -44.68) * mm, "end": v(60, -40.3) * mm});
            skArc(sketch, "E79.19", {"start": v(-56.15, -48.18) * mm, "mid": v(0, -67.5) * mm, "end": v(56.15, -48.18) * mm});
            skLineSegment(sketch, "E80", {"start": v(0, 90) * mm, "end": v(0, 120) * mm, "construction": true});
            skCircle(sketch, "E81", {"center": v(0, 120) * mm, "radius": 6 * mm});
            skArc(sketch, "E82", {"start": v(-15, 120) * mm, "mid": v(0, 135) * mm, "end": v(15, 120) * mm});
            skLineSegment(sketch, "E83", {"start": v(-15, 120) * mm, "end": v(-15, 108) * mm});
            skLineSegment(sketch, "E84", {"start": v(-15, 108) * mm, "end": v(-33, 90) * mm});
            skLineSegment(sketch, "E85", {"start": v(15, 120) * mm, "end": v(15, 108) * mm});
            skLineSegment(sketch, "E86", {"start": v(15, 108) * mm, "end": v(33, 90) * mm});
            skLineSegment(sketch, "E87", {"start": v(-80, 0) * mm, "end": v(80, 0) * mm, "construction": true});
            skLineSegment(sketch, "E88.MirrorCS", {"start": v(0, -90) * mm, "end": v(0, -120) * mm, "construction": true});
            skLineSegment(sketch, "E89.MirrorCS", {"start": v(-15, -108) * mm, "end": v(-33, -90) * mm});
            skArc(sketch, "E90.MirrorCS", {"start": v(-15, -120) * mm, "mid": v(0, -135) * mm, "end": v(15, -120) * mm});
            skLineSegment(sketch, "E91.MirrorCS", {"start": v(-15, -120) * mm, "end": v(-15, -108) * mm});
            skCircle(sketch, "E92.MirrorC", {"center": v(0, -120) * mm, "radius": 6 * mm});
            skLineSegment(sketch, "E93.MirrorCS", {"start": v(15, -120) * mm, "end": v(15, -108) * mm});
            skLineSegment(sketch, "E94.MirrorCS", {"start": v(15, -108) * mm, "end": v(33, -90) * mm});
            skSolve(sketch);
        }
        {
            var Q0;
            Q0 = qSketchRegion(id + "F16", true);
            var Q1;
            Q1=makeQuery(id+"F2.opExtrude","CAP_FACE",FACE,{"disambiguationData":[OSD([sQuery(id+"F0.wireOp",EDGE,"E12"),sQuery(id+"F0.wireOp",EDGE,"E13"),sQuery(id+"F0.wireOp",EDGE,"E14"),sQuery(id+"F0.wireOp",EDGE,"E15"),sQuery(id+"F0.wireOp",EDGE,"E17.filletArc"),sQuery(id+"F0.wireOp",EDGE,"E18.filletArc"),sQuery(id+"F0.wireOp",EDGE,"E19.filletArc"),sQuery(id+"F0.wireOp",EDGE,"E20.filletArc"),sQuery(id+"F0.wireOp",EDGE,"E25.0"),sQuery(id+"F0.wireOp",EDGE,"E25.1"),sQuery(id+"F0.wireOp",EDGE,"E25.2"),sQuery(id+"F0.wireOp",EDGE,"E25.3"),sQuery(id+"F0.wireOp",EDGE,"E25.4"),sQuery(id+"F0.wireOp",EDGE,"E25.5"),sQuery(id+"F0.wireOp",EDGE,"E25.6"),sQuery(id+"F0.wireOp",EDGE,"E25.7")])],"isStart":false});
            extrude(context, id + "F17", {"entities" : qUnion([Q0]), "endBound" : BoundingType.UP_TO_SURFACE, "endBoundEntityFace" : qUnion([Q1]), "depth" : 25 * mm});
        }
    });
